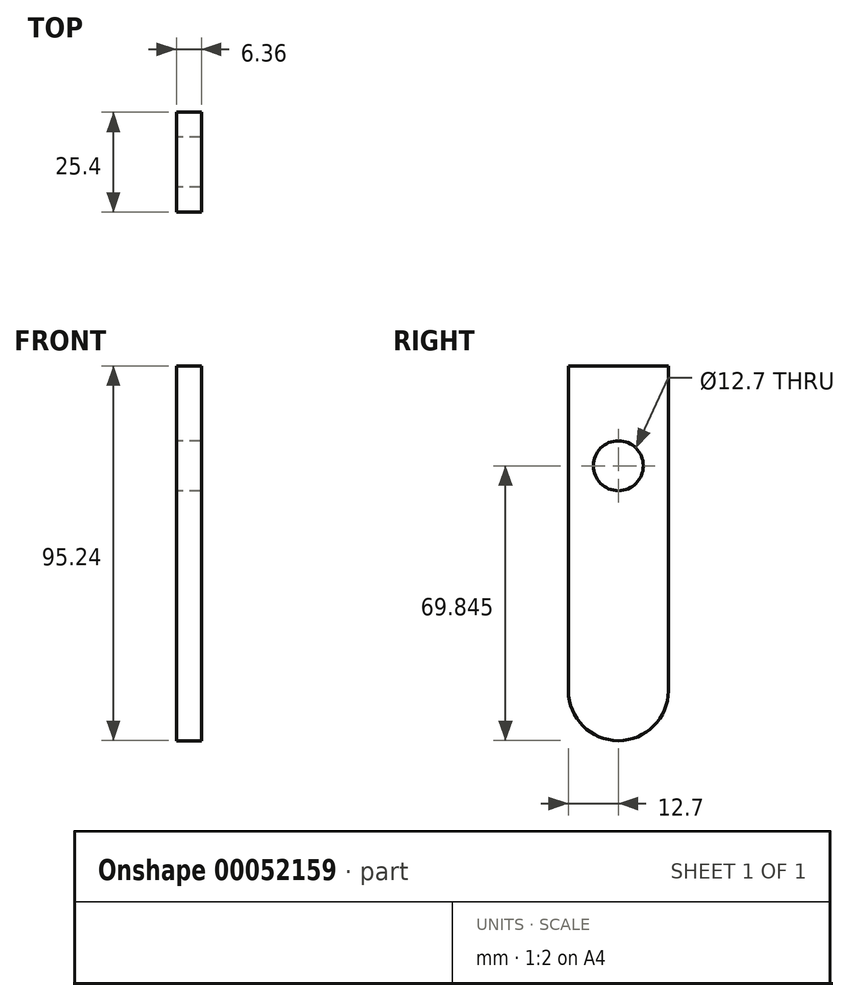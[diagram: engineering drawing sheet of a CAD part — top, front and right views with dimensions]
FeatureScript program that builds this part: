
annotation { "Feature Type Name" : "Feature", "Feature Type Description" : "" }
export const myFeature = defineFeature(function(context is Context, id is Id, definition is map)
    precondition{}
    {
        {
            var Q0;
            Q0=qCreatedBy(makeId("Right.planeOp"),FACE);
            var sketch = newSketch(context, id + "F0", { "sketchPlane" : qUnion([Q0])});
            skLineSegment(sketch, "E0.rect.bottom", {"start": v(12.7, 47.63) * mm, "end": v(-12.7, 47.63) * mm});
            skLineSegment(sketch, "E0.rect.top", {"start": v(12.7, -47.63) * mm, "end": v(-12.7, -47.63) * mm});
            skLineSegment(sketch, "E0.rect.left", {"start": v(12.7, 47.63) * mm, "end": v(12.7, -47.63) * mm});
            skLineSegment(sketch, "E0.rect.right", {"start": v(-12.7, 47.63) * mm, "end": v(-12.7, -47.63) * mm});
            skPoint(sketch, "E0.rect.middle", {"position": v(0, 0) * mm});
            skCircle(sketch, "E1", {"center": v(0, 22.23) * mm, "radius": 6.35 * mm});
            skSolve(sketch);
        }
        {
            var Q0;
            Q0=makeQuery(id+"F0.imprint","IMPRINT",FACE,{"disambiguationData":[TD([[makeQuery(id+"F0.imprint","IMPRINT",EDGE,{"derivedFrom":sQuery(id+"F0.wireOp",EDGE,"E0.rect.bottom")}),1.0]])]});
            extrude(context, id + "F1", {"entities" : qUnion([Q0]), "endBound" : BoundingType.SYMMETRIC, "depth" : 6.35 * mm});
        }
        {
            var Q0;
            Q0=makeQuery(id+"F1.opExtrude","SWEPT_EDGE",EDGE,{"disambiguationData":[OSD([sQuery(id+"F0.wireOp",EDGE,"E0.rect.top"),sQuery(id+"F0.wireOp",EDGE,"E0.rect.left")])]});
            var Q1;
            Q1=makeQuery(id+"F1.opExtrude","SWEPT_EDGE",EDGE,{"disambiguationData":[OSD([sQuery(id+"F0.wireOp",EDGE,"E0.rect.top"),sQuery(id+"F0.wireOp",EDGE,"E0.rect.right")])]});
            fillet(context, id + "F2", {"entities" : qUnion([Q0, Q1]), "radius" : 12.7 * mm, "tangentPropagation" : true, "allowEdgeOverflow" : false});
        }
    });
